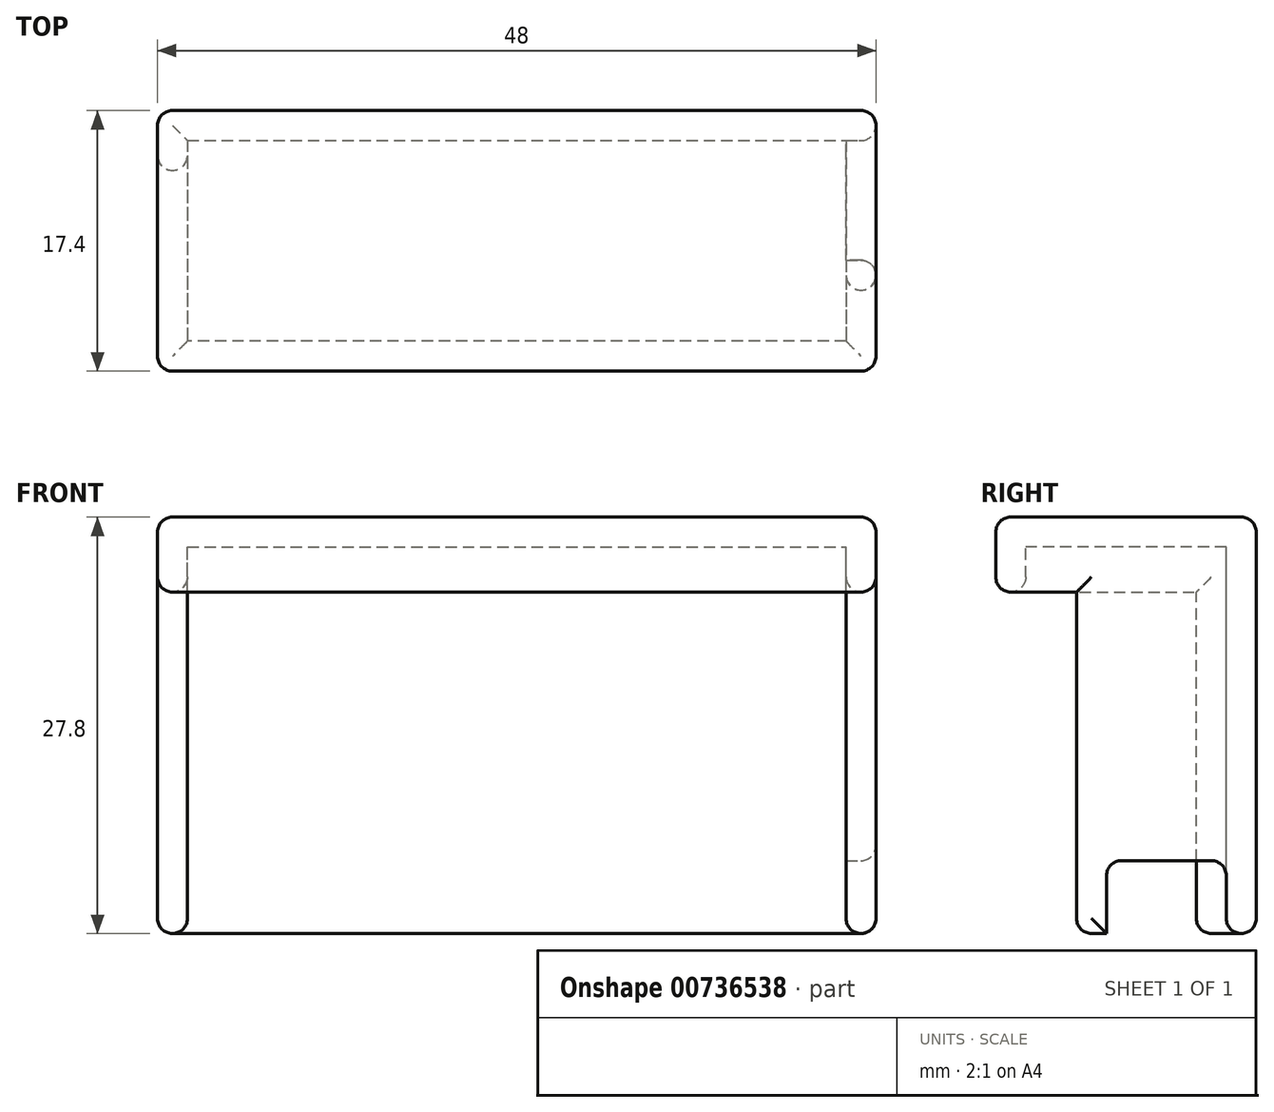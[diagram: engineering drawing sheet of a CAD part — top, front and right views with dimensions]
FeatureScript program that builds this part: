
annotation { "Feature Type Name" : "Feature", "Feature Type Description" : "" }
export const myFeature = defineFeature(function(context is Context, id is Id, definition is map)
    precondition{}
    {
        {
            var Q0;
            Q0=qCreatedBy(makeId("Front.planeOp"),FACE);
            var sketch = newSketch(context, id + "F0", { "sketchPlane" : qUnion([Q0])});
            skLineSegment(sketch, "E0.bottom", {"start": v(0, 0) * mm, "end": v(48, 0) * mm});
            skLineSegment(sketch, "E0.top", {"start": v(0, 27.8) * mm, "end": v(48, 27.8) * mm});
            skLineSegment(sketch, "E0.left", {"start": v(0, 0) * mm, "end": v(0, 27.8) * mm});
            skLineSegment(sketch, "E0.right", {"start": v(48, 0) * mm, "end": v(48, 27.8) * mm});
            skSolve(sketch);
        }
        {
            var Q0;
            Q0 = qSketchRegion(id + "F0", true);
            extrude(context, id + "F1", {"entities" : qUnion([Q0]), "depth" : 2 * mm, "offsetDistance" : 25 * mm});
        }
        {
            var Q0;
            Q0=makeQuery(id+"F1.opExtrude","CAP_FACE",FACE,{"disambiguationData":[OSD([sQuery(id+"F0.wireOp",EDGE,"E0.bottom"),sQuery(id+"F0.wireOp",EDGE,"E0.top"),sQuery(id+"F0.wireOp",EDGE,"E0.left"),sQuery(id+"F0.wireOp",EDGE,"E0.right")])],"isStart":false});
            var sketch = newSketch(context, id + "F2", { "sketchPlane" : qUnion([Q0])});
            skLineSegment(sketch, "E1.bottom", {"start": v(0, 27.8) * mm, "end": v(48, 27.8) * mm});
            skLineSegment(sketch, "E1.top", {"start": v(0, 25.8) * mm, "end": v(48, 25.8) * mm});
            skLineSegment(sketch, "E1.left", {"start": v(0, 27.8) * mm, "end": v(0, 25.8) * mm});
            skLineSegment(sketch, "E1.right", {"start": v(48, 27.8) * mm, "end": v(48, 25.8) * mm});
            skSolve(sketch);
        }
        {
            var Q0;
            Q0 = qSketchRegion(id + "F2", true);
            extrude(context, id + "F3", {"entities" : qUnion([Q0]), "operationType" : NewBodyOperationType.ADD, "depth" : 15.4 * mm, "offsetDistance" : 25 * mm});
        }
        {
            var Q0;
            Q0=makeQuery(id+"F3.opExtrude","SWEPT_FACE",FACE,{"disambiguationData":[OSD([sQuery(id+"F2.wireOp",EDGE,"E1.top")])]});
            var sketch = newSketch(context, id + "F4", { "sketchPlane" : qUnion([Q0])});
            skLineSegment(sketch, "E2.bottom", {"start": v(48, 2) * mm, "end": v(46, 2) * mm});
            skLineSegment(sketch, "E2.top", {"start": v(48, 12) * mm, "end": v(46, 12) * mm});
            skLineSegment(sketch, "E2.left", {"start": v(48, 2) * mm, "end": v(48, 12) * mm});
            skLineSegment(sketch, "E2.right", {"start": v(46, 2) * mm, "end": v(46, 12) * mm});
            skLineSegment(sketch, "E3.bottom", {"start": v(0, 2) * mm, "end": v(2, 2) * mm});
            skLineSegment(sketch, "E3.top", {"start": v(0, 4) * mm, "end": v(2, 4) * mm});
            skLineSegment(sketch, "E3.left", {"start": v(0, 2) * mm, "end": v(0, 4) * mm});
            skLineSegment(sketch, "E3.right", {"start": v(2, 2) * mm, "end": v(2, 4) * mm});
            skSolve(sketch);
        }
        {
            var Q0;
            Q0 = qSketchRegion(id + "F4", true);
            extrude(context, id + "F5", {"entities" : qUnion([Q0]), "operationType" : NewBodyOperationType.ADD, "depth" : 25.8 * mm, "offsetDistance" : 25 * mm});
        }
        {
            var Q0;
            Q0=makeQuery(id+"F3.opExtrude","SWEPT_FACE",FACE,{"disambiguationData":[OSD([sQuery(id+"F2.wireOp",EDGE,"E1.top")])]});
            var sketch = newSketch(context, id + "F6", { "sketchPlane" : qUnion([Q0])});
            skLineSegment(sketch, "E4.bottom", {"start": v(46, 12) * mm, "end": v(48, 12) * mm});
            skLineSegment(sketch, "E4.top", {"start": v(46, 17.4) * mm, "end": v(48, 17.4) * mm});
            skLineSegment(sketch, "E4.right", {"start": v(48, 12) * mm, "end": v(48, 17.4) * mm});
            skLineSegment(sketch, "E5.bottom", {"start": v(2, 4) * mm, "end": v(0, 4) * mm});
            skLineSegment(sketch, "E5.top", {"start": v(2, 17.4) * mm, "end": v(0, 17.4) * mm});
            skLineSegment(sketch, "E5.right", {"start": v(0, 4) * mm, "end": v(0, 17.4) * mm});
            skLineSegment(sketch, "E6", {"start": v(46, 15.4) * mm, "end": v(2, 15.4) * mm});
            skLineSegment(sketch, "E7", {"start": v(46, 17.4) * mm, "end": v(0, 17.4) * mm});
            skLineSegment(sketch, "E8", {"start": v(46, 12) * mm, "end": v(46, 15.4) * mm});
            skLineSegment(sketch, "E9", {"start": v(2, 4) * mm, "end": v(2, 15.4) * mm});
            skSolve(sketch);
        }
        {
            var Q0;
            Q0 = qSketchRegion(id + "F6", true);
            extrude(context, id + "F7", {"entities" : qUnion([Q0]), "operationType" : NewBodyOperationType.ADD, "depth" : 3 * mm, "offsetDistance" : 25 * mm});
        }
        {
            var Q0;
            Q0=makeQuery(id+"F7.boolean.opBoolean","MERGE",FACE,{"derivedFrom":[makeQuery(id+"F5.boolean.opBoolean","MERGE",FACE,{"derivedFrom":[makeQuery(id+"F3.boolean.opBoolean","MERGE",FACE,{"derivedFrom":[makeQuery(id+"F1.opExtrude","SWEPT_FACE",FACE,{"disambiguationData":[OSD([sQuery(id+"F0.wireOp",EDGE,"E0.right")])]}),makeQuery(id+"F3.opExtrude","SWEPT_FACE",FACE,{"disambiguationData":[OSD([sQuery(id+"F2.wireOp",EDGE,"E1.right")])]})]}),makeQuery(id+"F5.opExtrude","SWEPT_FACE",FACE,{"disambiguationData":[OSD([sQuery(id+"F4.wireOp",EDGE,"E2.left")])]})]}),makeQuery(id+"F7.opExtrude","SWEPT_FACE",FACE,{"disambiguationData":[OSD([sQuery(id+"F6.wireOp",EDGE,"E4.right")])]})]});
            var sketch = newSketch(context, id + "F8", { "sketchPlane" : qUnion([Q0])});
            skLineSegment(sketch, "E10.right", {"start": v(-10, 0) * mm, "end": v(-10, 4.86) * mm});
            skLineSegment(sketch, "E11", {"start": v(-10, 0) * mm, "end": v(-2, 0) * mm});
            skLineSegment(sketch, "E12", {"start": v(-10, 4.86) * mm, "end": v(-2, 4.86) * mm});
            skLineSegment(sketch, "E13", {"start": v(-2, 4.86) * mm, "end": v(-2, 0) * mm});
            skSolve(sketch);
        }
        {
            var Q0;
            Q0 = qSketchRegion(id + "F8", true);
            extrude(context, id + "F9", {"entities" : qUnion([Q0]), "operationType" : NewBodyOperationType.REMOVE, "oppositeDirection" : true, "depth" : 2 * mm, "offsetDistance" : 25 * mm});
        }
        {
            var Q0;
            Q0=makeQuery(id+"F3.boolean.opBoolean","MERGE",FACE,{"derivedFrom":[makeQuery(id+"F1.opExtrude","SWEPT_FACE",FACE,{"disambiguationData":[OSD([sQuery(id+"F0.wireOp",EDGE,"E0.top")])]}),makeQuery(id+"F3.opExtrude","SWEPT_FACE",FACE,{"disambiguationData":[OSD([sQuery(id+"F2.wireOp",EDGE,"E1.bottom")])]})]});
            var Q1;
            Q1=makeQuery(id+"F7.boolean.opBoolean","MERGE",FACE,{"derivedFrom":[makeQuery(id+"F5.boolean.opBoolean","MERGE",FACE,{"derivedFrom":[makeQuery(id+"F3.boolean.opBoolean","MERGE",FACE,{"derivedFrom":[makeQuery(id+"F1.opExtrude","SWEPT_FACE",FACE,{"disambiguationData":[OSD([sQuery(id+"F0.wireOp",EDGE,"E0.right")])]}),makeQuery(id+"F3.opExtrude","SWEPT_FACE",FACE,{"disambiguationData":[OSD([sQuery(id+"F2.wireOp",EDGE,"E1.right")])]})]}),makeQuery(id+"F5.opExtrude","SWEPT_FACE",FACE,{"disambiguationData":[OSD([sQuery(id+"F4.wireOp",EDGE,"E2.left")])]})]}),makeQuery(id+"F7.opExtrude","SWEPT_FACE",FACE,{"disambiguationData":[OSD([sQuery(id+"F6.wireOp",EDGE,"E4.right")])]})]});
            var Q2;
            Q2=makeQuery(id+"F1.opExtrude","CAP_FACE",FACE,{"disambiguationData":[OSD([sQuery(id+"F0.wireOp",EDGE,"E0.bottom"),sQuery(id+"F0.wireOp",EDGE,"E0.top"),sQuery(id+"F0.wireOp",EDGE,"E0.left"),sQuery(id+"F0.wireOp",EDGE,"E0.right")])],"isStart":true});
            var Q3;
            Q3=makeQuery(id+"F7.boolean.opBoolean","MERGE",FACE,{"derivedFrom":[makeQuery(id+"F3.opExtrude","CAP_FACE",FACE,{"disambiguationData":[OSD([sQuery(id+"F2.wireOp",EDGE,"E1.bottom"),sQuery(id+"F2.wireOp",EDGE,"E1.top"),sQuery(id+"F2.wireOp",EDGE,"E1.left"),sQuery(id+"F2.wireOp",EDGE,"E1.right")])],"isStart":false}),makeQuery(id+"F7.opExtrude","SWEPT_FACE",FACE,{"disambiguationData":[OSD([sQuery(id+"F6.wireOp",EDGE,"E4.top"),sQuery(id+"F6.wireOp",EDGE,"E7")])]})]});
            var Q4;
            Q4=makeQuery(id+"F7.boolean.opBoolean","MERGE",FACE,{"derivedFrom":[makeQuery(id+"F5.boolean.opBoolean","MERGE",FACE,{"derivedFrom":[makeQuery(id+"F3.boolean.opBoolean","MERGE",FACE,{"derivedFrom":[makeQuery(id+"F1.opExtrude","SWEPT_FACE",FACE,{"disambiguationData":[OSD([sQuery(id+"F0.wireOp",EDGE,"E0.left")])]}),makeQuery(id+"F3.opExtrude","SWEPT_FACE",FACE,{"disambiguationData":[OSD([sQuery(id+"F2.wireOp",EDGE,"E1.left")])]})]}),makeQuery(id+"F5.opExtrude","SWEPT_FACE",FACE,{"disambiguationData":[OSD([sQuery(id+"F4.wireOp",EDGE,"E3.left")])]})]}),makeQuery(id+"F7.opExtrude","SWEPT_FACE",FACE,{"disambiguationData":[OSD([sQuery(id+"F6.wireOp",EDGE,"E5.right")])]})]});
            var Q5;
            Q5=makeQuery(id+"F9.boolean.opBoolean","COPY",EDGE,{"derivedFrom":makeQuery(id+"F9.opExtrude","SWEPT_EDGE",EDGE,{"disambiguationData":[OSD([sQuery(id+"F8.wireOp",EDGE,"E12"),sQuery(id+"F8.wireOp",EDGE,"E13")])]})});
            var Q6;
            Q6=makeQuery(id+"F9.boolean.opBoolean","COPY",EDGE,{"derivedFrom":makeQuery(id+"F9.opExtrude","SWEPT_EDGE",EDGE,{"disambiguationData":[OSD([sQuery(id+"F8.wireOp",EDGE,"E10.right"),sQuery(id+"F8.wireOp",EDGE,"E12")])]})});
            var Q7;
            Q7=makeQuery(id+"F5.opExtrude","SWEPT_EDGE",EDGE,{"disambiguationData":[OSD([sQuery(id+"F4.wireOp",EDGE,"E2.top"),sQuery(id+"F4.wireOp",EDGE,"E2.right")])]});
            var Q8;
            Q8=makeQuery(id+"F5.opExtrude","SWEPT_EDGE",EDGE,{"disambiguationData":[OSD([sQuery(id+"F4.wireOp",EDGE,"E3.top"),sQuery(id+"F4.wireOp",EDGE,"E3.right")])]});
            var Q9;
            Q9=makeQuery(id+"F7.opExtrude","CAP_EDGE",EDGE,{"disambiguationData":[OSD([sQuery(id+"F6.wireOp",EDGE,"E9")])],"isStart":false});
            var Q10;
            Q10=makeQuery(id+"F7.opExtrude","CAP_EDGE",EDGE,{"disambiguationData":[OSD([sQuery(id+"F6.wireOp",EDGE,"E8")])],"isStart":false});
            var Q11;
            Q11=makeQuery(id+"F7.opExtrude","CAP_EDGE",EDGE,{"disambiguationData":[OSD([sQuery(id+"F6.wireOp",EDGE,"E6")])],"isStart":false});
            var Q12;
            Q12=makeQuery(id+"F5.opExtrude","CAP_EDGE",EDGE,{"disambiguationData":[OSD([sQuery(id+"F4.wireOp",EDGE,"E3.top")])],"isStart":false});
            var Q13;
            {var subQ0=sQuery(id+"F0.wireOp",EDGE,"E0.bottom");Q13=makeQuery(id+"F9.boolean.opBoolean","MERGE",EDGE,{"derivedFrom":[makeQuery(id+"F1.opExtrude","CAP_EDGE",EDGE,{"disambiguationData":[OSD([subQ0])],"isStart":false}),makeQuery(id+"F9.opExtrude","SWEPT_EDGE",EDGE,{"disambiguationData":[OSD([subQ0,sQuery(id+"F0.wireOp",EDGE,"E0.right"),sQuery(id+"F4.wireOp",EDGE,"E2.left"),sQuery(id+"F8.wireOp",EDGE,"E11"),sQuery(id+"F8.wireOp",EDGE,"E13")])]})]});}
            var Q14;
            Q14=makeQuery(id+"F9.boolean.opBoolean","COPY",EDGE,{"derivedFrom":makeQuery(id+"F9.opExtrude","SWEPT_EDGE",EDGE,{"disambiguationData":[OSD([sQuery(id+"F0.wireOp",EDGE,"E0.bottom"),sQuery(id+"F0.wireOp",EDGE,"E0.right"),sQuery(id+"F4.wireOp",EDGE,"E2.left"),sQuery(id+"F8.wireOp",EDGE,"E10.right"),sQuery(id+"F8.wireOp",EDGE,"E11")])]})});
            var Q15;
            Q15=makeQuery(id+"F5.opExtrude","CAP_EDGE",EDGE,{"disambiguationData":[OSD([sQuery(id+"F4.wireOp",EDGE,"E2.right")])],"isStart":false});
            var Q16;
            Q16=makeQuery(id+"F5.opExtrude","CAP_EDGE",EDGE,{"disambiguationData":[OSD([sQuery(id+"F4.wireOp",EDGE,"E3.right")])],"isStart":false});
            var Q17;
            Q17=makeQuery(id+"F5.opExtrude","CAP_EDGE",EDGE,{"disambiguationData":[OSD([sQuery(id+"F4.wireOp",EDGE,"E2.top")])],"isStart":false});
            fillet(context, id + "F10", {"entities" : qUnion([Q0, Q1, Q2, Q3, Q4, Q5, Q6, Q7, Q8, Q9, Q10, Q11, Q12, Q13, Q14, Q15, Q16, Q17]), "radius" : 1 * mm, "tangentPropagation" : true, "allowEdgeOverflow" : false});
        }
    });
